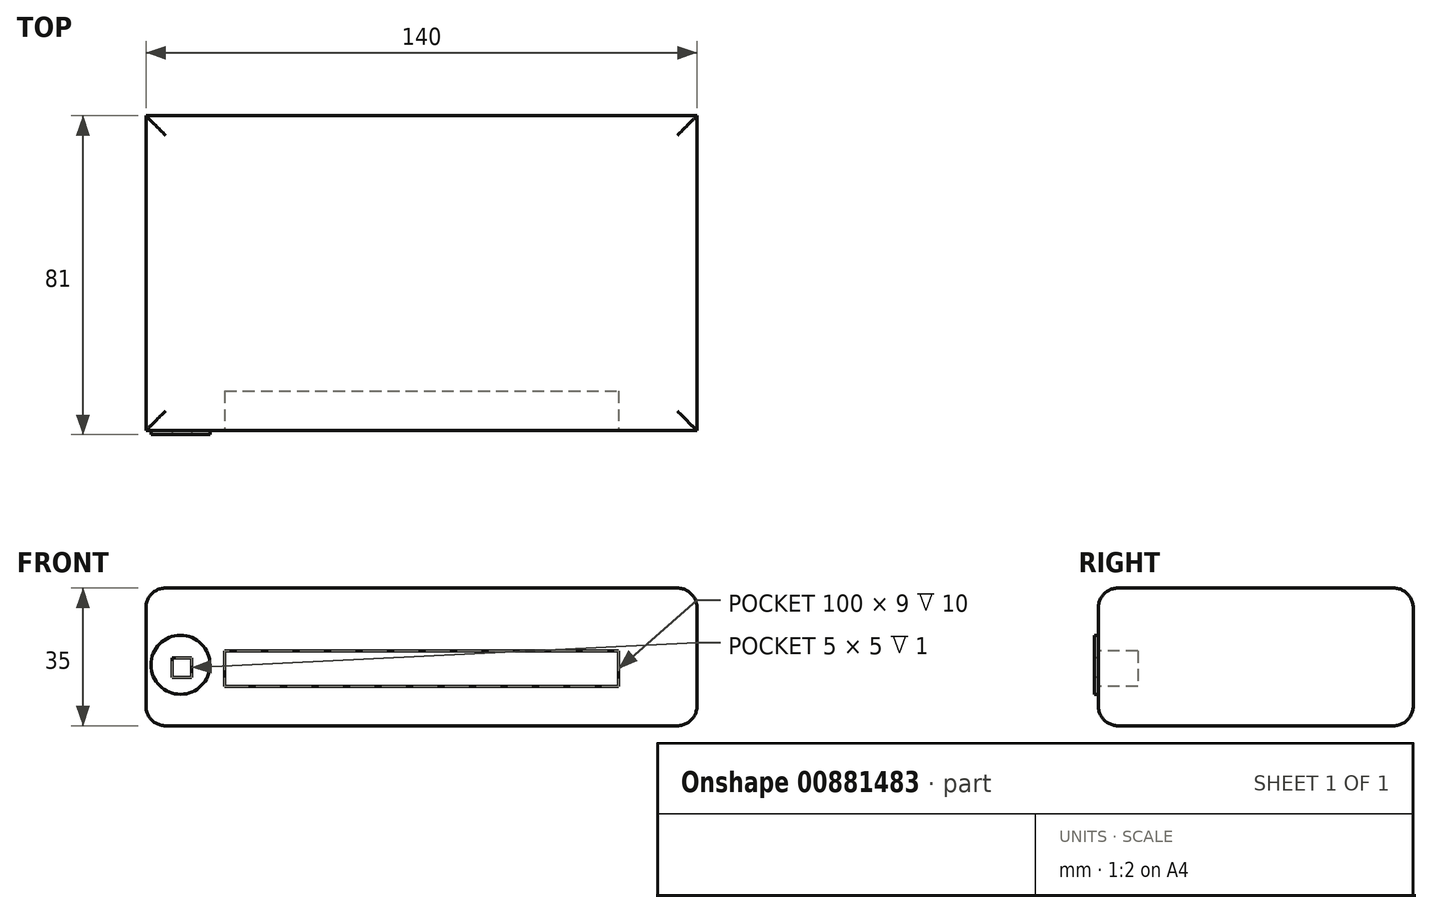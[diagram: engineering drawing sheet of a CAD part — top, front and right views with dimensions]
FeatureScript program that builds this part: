
annotation { "Feature Type Name" : "Feature", "Feature Type Description" : "" }
export const myFeature = defineFeature(function(context is Context, id is Id, definition is map)
    precondition{}
    {
        {
            var Q0;
            Q0=qCreatedBy(makeId("Top.planeOp"),FACE);
            var sketch = newSketch(context, id + "F0", { "sketchPlane" : qUnion([Q0])});
            skLineSegment(sketch, "E0.bottom", {"start": v(-64.84, 28.5) * mm, "end": v(75.16, 28.5) * mm});
            skLineSegment(sketch, "E0.top", {"start": v(-64.84, -51.5) * mm, "end": v(75.16, -51.5) * mm});
            skLineSegment(sketch, "E0.left", {"start": v(-64.84, 28.5) * mm, "end": v(-64.84, -51.5) * mm});
            skLineSegment(sketch, "E0.right", {"start": v(75.16, 28.5) * mm, "end": v(75.16, -51.5) * mm});
            skSolve(sketch);
        }
        {
            var Q0;
            Q0=makeQuery(id+"F0.imprint","IMPRINT",FACE,{"disambiguationData":[TD([[makeQuery(id+"F0.imprint","IMPRINT",EDGE,{"derivedFrom":sQuery(id+"F0.wireOp",EDGE,"E0.bottom")}),-1.0]])]});
            extrude(context, id + "F1", {"entities" : qUnion([Q0]), "depth" : 35 * mm, "offsetDistance" : 25 * mm});
        }
        {
            var Q0;
            Q0=makeQuery(id+"F1.opExtrude","SWEPT_FACE",FACE,{"disambiguationData":[OSD([sQuery(id+"F0.wireOp",EDGE,"E0.top")])]});
            var sketch = newSketch(context, id + "F2", { "sketchPlane" : qUnion([Q0])});
            skLineSegment(sketch, "E1.bottom", {"start": v(-44.84, 19) * mm, "end": v(55.16, 19) * mm});
            skLineSegment(sketch, "E1.top", {"start": v(-44.84, 10) * mm, "end": v(55.16, 10) * mm});
            skLineSegment(sketch, "E1.left", {"start": v(-44.84, 19) * mm, "end": v(-44.84, 10) * mm});
            skLineSegment(sketch, "E1.right", {"start": v(55.16, 19) * mm, "end": v(55.16, 10) * mm});
            skSolve(sketch);
        }
        {
            var Q0;
            Q0=makeQuery(id+"F2.imprint","IMPRINT",FACE,{"disambiguationData":[TD([[makeQuery(id+"F2.imprint","IMPRINT",EDGE,{"derivedFrom":sQuery(id+"F2.wireOp",EDGE,"E1.bottom")}),-1.0]])]});
            extrude(context, id + "F3", {"entities" : qUnion([Q0]), "operationType" : NewBodyOperationType.REMOVE, "oppositeDirection" : true, "depth" : 10 * mm, "offsetDistance" : 25 * mm});
        }
        {
            var Q0;
            Q0=makeQuery(id+"F3.boolean.opBoolean","COPY",FACE,{"derivedFrom":makeQuery(id+"F3.opExtrude","CAP_FACE",FACE,{"disambiguationData":[OSD([sQuery(id+"F2.wireOp",EDGE,"E1.bottom"),sQuery(id+"F2.wireOp",EDGE,"E1.top"),sQuery(id+"F2.wireOp",EDGE,"E1.left"),sQuery(id+"F2.wireOp",EDGE,"E1.right")])],"isStart":false})});
            var sketch = newSketch(context, id + "F4", { "sketchPlane" : qUnion([Q0])});
            skLineSegment(sketch, "E2.bottom", {"start": v(-44.84, 19) * mm, "end": v(55.16, 19) * mm});
            skLineSegment(sketch, "E2.top", {"start": v(-44.84, 10) * mm, "end": v(55.16, 10) * mm});
            skLineSegment(sketch, "E2.left", {"start": v(-44.84, 19) * mm, "end": v(-44.84, 10) * mm});
            skLineSegment(sketch, "E2.right", {"start": v(55.16, 19) * mm, "end": v(55.16, 10) * mm});
            skSolve(sketch);
        }
        {
            var Q0;
            Q0=makeQuery(id+"F1.opExtrude","CAP_EDGE",EDGE,{"disambiguationData":[OSD([sQuery(id+"F0.wireOp",EDGE,"E0.right")])],"isStart":true});
            var Q1;
            Q1=makeQuery(id+"F1.opExtrude","CAP_EDGE",EDGE,{"disambiguationData":[OSD([sQuery(id+"F0.wireOp",EDGE,"E0.top")])],"isStart":true});
            var Q2;
            Q2=makeQuery(id+"F1.opExtrude","CAP_EDGE",EDGE,{"disambiguationData":[OSD([sQuery(id+"F0.wireOp",EDGE,"E0.bottom")])],"isStart":true});
            var Q3;
            Q3=makeQuery(id+"F1.opExtrude","CAP_EDGE",EDGE,{"disambiguationData":[OSD([sQuery(id+"F0.wireOp",EDGE,"E0.left")])],"isStart":true});
            fillet(context, id + "F5", {"entities" : qUnion([Q0, Q1, Q2, Q3]), "radius" : 5 * mm, "tangentPropagation" : true, "allowEdgeOverflow" : false});
        }
        {
            var Q0;
            Q0=makeQuery(id+"F1.opExtrude","CAP_EDGE",EDGE,{"disambiguationData":[OSD([sQuery(id+"F0.wireOp",EDGE,"E0.left")])],"isStart":false});
            var Q1;
            Q1=makeQuery(id+"F1.opExtrude","CAP_EDGE",EDGE,{"disambiguationData":[OSD([sQuery(id+"F0.wireOp",EDGE,"E0.bottom")])],"isStart":false});
            var Q2;
            Q2=makeQuery(id+"F1.opExtrude","CAP_EDGE",EDGE,{"disambiguationData":[OSD([sQuery(id+"F0.wireOp",EDGE,"E0.top")])],"isStart":false});
            var Q3;
            Q3=makeQuery(id+"F1.opExtrude","CAP_FACE",FACE,{"disambiguationData":[OSD([sQuery(id+"F0.wireOp",EDGE,"E0.bottom"),sQuery(id+"F0.wireOp",EDGE,"E0.top"),sQuery(id+"F0.wireOp",EDGE,"E0.left"),sQuery(id+"F0.wireOp",EDGE,"E0.right")])],"isStart":false});
            fillet(context, id + "F6", {"entities" : qUnion([Q0, Q1, Q2, Q3]), "radius" : 5 * mm, "tangentPropagation" : true, "allowEdgeOverflow" : false});
        }
        {
            var Q0;
            Q0=makeQuery(id+"F1.opExtrude","SWEPT_FACE",FACE,{"disambiguationData":[OSD([sQuery(id+"F0.wireOp",EDGE,"E0.top")])]});
            var sketch = newSketch(context, id + "F7", { "sketchPlane" : qUnion([Q0])});
            skCircle(sketch, "E3", {"center": v(-56.06, 15.5) * mm, "radius": 7.5 * mm});
            skSolve(sketch);
        }
        {
            var Q0;
            Q0=makeQuery(id+"F7.imprint","IMPRINT",FACE,{"disambiguationData":[TD([[makeQuery(id+"F7.imprint","IMPRINT",EDGE,{"derivedFrom":sQuery(id+"F7.wireOp",EDGE,"E3")}),1.0]])]});
            extrude(context, id + "F8", {"entities" : qUnion([Q0]), "operationType" : NewBodyOperationType.ADD, "depth" : 1 * mm, "offsetDistance" : 25 * mm});
        }
        {
            var Q0;
            Q0=makeQuery(id+"F8.opExtrude","CAP_FACE",FACE,{"disambiguationData":[OSD([sQuery(id+"F7.wireOp",EDGE,"E3")])],"isStart":false});
            var sketch = newSketch(context, id + "F9", { "sketchPlane" : qUnion([Q0])});
            skLineSegment(sketch, "E4.bottom", {"start": v(-58.24, 17.29) * mm, "end": v(-53.24, 17.29) * mm});
            skLineSegment(sketch, "E4.top", {"start": v(-58.24, 12.29) * mm, "end": v(-53.24, 12.29) * mm});
            skLineSegment(sketch, "E4.left", {"start": v(-58.24, 17.29) * mm, "end": v(-58.24, 12.29) * mm});
            skLineSegment(sketch, "E4.right", {"start": v(-53.24, 17.29) * mm, "end": v(-53.24, 12.29) * mm});
            skSolve(sketch);
        }
        {
            var Q0;
            Q0=makeQuery(id+"F9.imprint","IMPRINT",FACE,{"disambiguationData":[TD([[makeQuery(id+"F9.imprint","IMPRINT",EDGE,{"derivedFrom":sQuery(id+"F9.wireOp",EDGE,"E4.bottom")}),-1.0]])]});
            extrude(context, id + "F10", {"entities" : qUnion([Q0]), "operationType" : NewBodyOperationType.REMOVE, "oppositeDirection" : true, "depth" : 1 * mm, "offsetDistance" : 25 * mm});
        }
    });
